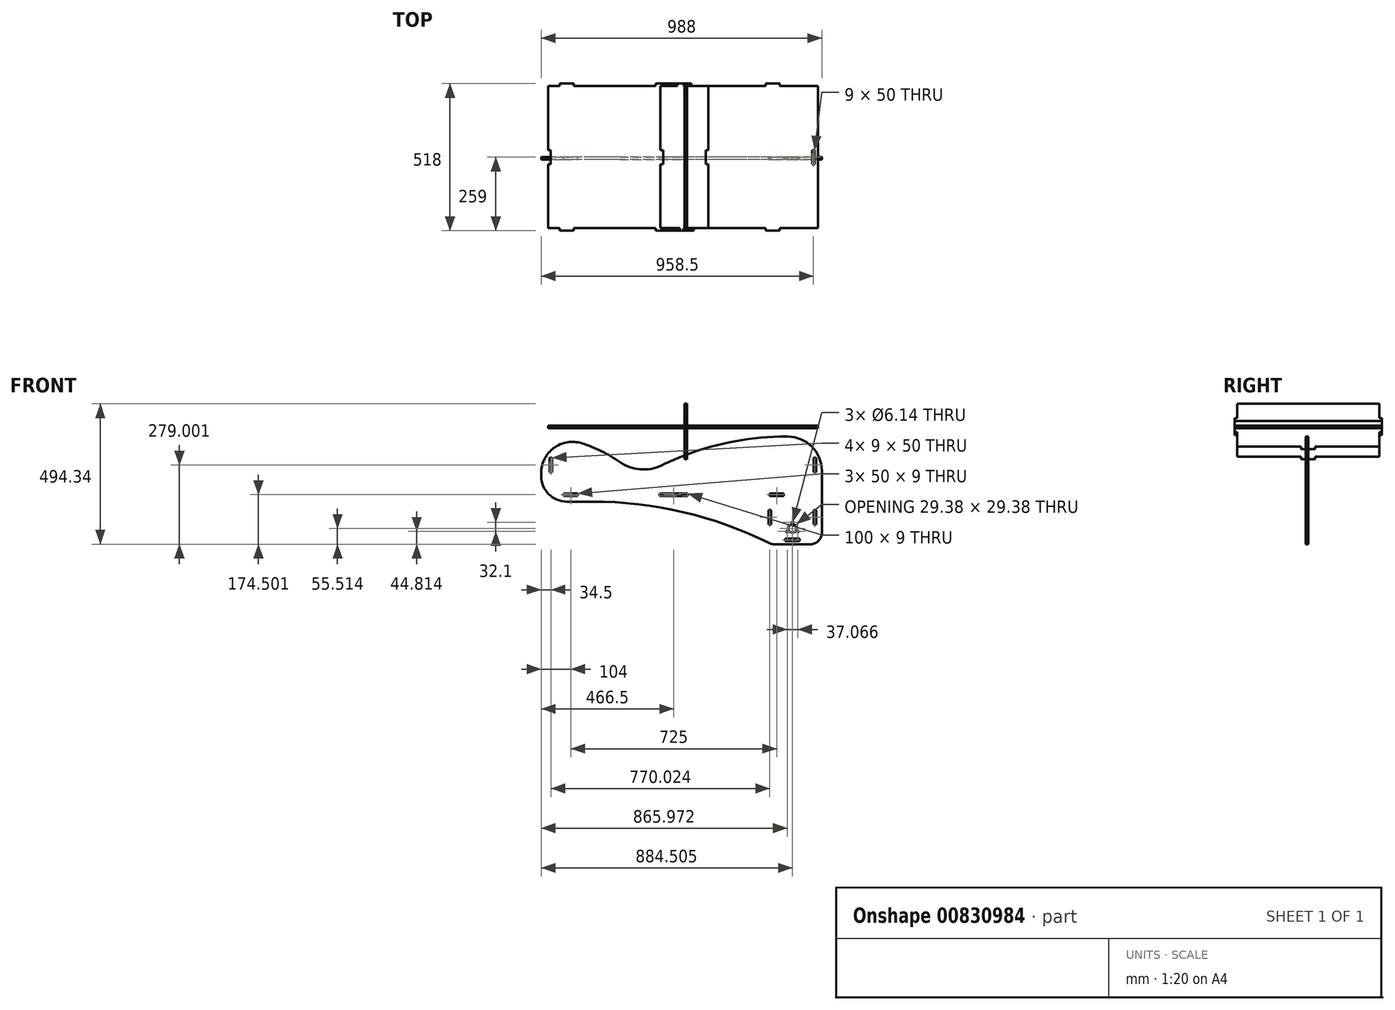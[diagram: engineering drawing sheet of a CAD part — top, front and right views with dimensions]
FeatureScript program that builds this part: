
annotation { "Feature Type Name" : "Feature", "Feature Type Description" : "" }
export const myFeature = defineFeature(function(context is Context, id is Id, definition is map)
    precondition{}
    {
        {
            var Q0;
            Q0=qCreatedBy(makeId("Front.planeOp"),FACE);
            var sketch = newSketch(context, id + "F0", { "sketchPlane" : qUnion([Q0])});
            skPoint(sketch, "E0.middle", {"position": v(0, 0) * mm});
            skLineSegment(sketch, "E1", {"start": v(-87.5, -229.84) * mm, "end": v(-87.5, -238.84) * mm});
            skLineSegment(sketch, "E2", {"start": v(-87.5, -238.84) * mm, "end": v(12.5, -238.84) * mm});
            skLineSegment(sketch, "E3", {"start": v(12.5, -238.84) * mm, "end": v(12.5, -229.84) * mm});
            skLineSegment(sketch, "E4", {"start": v(-425, -229.84) * mm, "end": v(-425, -238.84) * mm});
            skLineSegment(sketch, "E5", {"start": v(-425, -238.84) * mm, "end": v(-375, -238.84) * mm});
            skLineSegment(sketch, "E6", {"start": v(-375, -238.84) * mm, "end": v(-375, -229.84) * mm});
            skLineSegment(sketch, "E7", {"start": v(-425, -229.84) * mm, "end": v(-375, -229.84) * mm});
            skLineSegment(sketch, "E8", {"start": v(-465, -229.84) * mm, "end": v(-465, -230) * mm});
            skLineSegment(sketch, "E9", {"start": v(455.02, -288.84) * mm, "end": v(455.02, -338.84) * mm});
            skLineSegment(sketch, "E10", {"start": v(405.02, -388.84) * mm, "end": v(355.02, -388.84) * mm});
            skLineSegment(sketch, "E11", {"start": v(305.02, -338.84) * mm, "end": v(305.02, -288.84) * mm});
            skLineSegment(sketch, "E12", {"start": v(305.02, -288.84) * mm, "end": v(296.02, -288.84) * mm});
            skLineSegment(sketch, "E13", {"start": v(296.02, -288.84) * mm, "end": v(296.02, -338.84) * mm});
            skLineSegment(sketch, "E14", {"start": v(296.02, -338.84) * mm, "end": v(305.02, -338.84) * mm});
            skLineSegment(sketch, "E15", {"start": v(455.02, -288.84) * mm, "end": v(464.02, -288.84) * mm});
            skLineSegment(sketch, "E16", {"start": v(464.02, -288.84) * mm, "end": v(464.02, -338.84) * mm});
            skLineSegment(sketch, "E17", {"start": v(464.02, -338.84) * mm, "end": v(455.02, -338.84) * mm});
            skLineSegment(sketch, "E18", {"start": v(355.02, -388.84) * mm, "end": v(355.02, -397.84) * mm});
            skLineSegment(sketch, "E19", {"start": v(355.02, -397.84) * mm, "end": v(405.02, -397.84) * mm});
            skLineSegment(sketch, "E20", {"start": v(405.02, -397.84) * mm, "end": v(405.02, -388.84) * mm});
            skPoint(sketch, "E21.start.orphan", {"position": v(380.84, -337.36) * mm});
            skLineSegment(sketch, "E22", {"start": v(380.5, -388.84) * mm, "end": v(380.5, -328.86) * mm});
            skCircle(sketch, "E23", {"center": v(380.5, -353.33) * mm, "radius": 14.7 * mm});
            skCircle(sketch, "E24", {"center": v(380.5, -331.93) * mm, "radius": 3.07 * mm});
            skPoint(sketch, "E24.second.point", {"position": v(380.5, -328.86) * mm});
            skPoint(sketch, "E24.third.point", {"position": v(377.5, -331.28) * mm});
            skPoint(sketch, "E25.end.orphan", {"position": v(380.5, -335) * mm});
            skPoint(sketch, "E25.start.orphan", {"position": v(380.5, -338.64) * mm});
            skCircle(sketch, "E26.1.0", {"center": v(361.97, -364.03) * mm, "radius": 3.07 * mm});
            skPoint(sketch, "E26.1.1", {"position": v(359.31, -365.56) * mm});
            skPoint(sketch, "E26.1.2", {"position": v(362.92, -366.95) * mm});
            skPoint(sketch, "E26.1.3", {"position": v(364.63, -362.5) * mm});
            skCircle(sketch, "E26.2.0", {"center": v(399.04, -364.03) * mm, "radius": 3.07 * mm});
            skPoint(sketch, "E26.2.1", {"position": v(401.7, -365.56) * mm});
            skPoint(sketch, "E26.2.2", {"position": v(401.1, -361.75) * mm});
            skPoint(sketch, "E26.2.3", {"position": v(396.38, -362.5) * mm});
            skLineSegment(sketch, "E27", {"start": v(484, -338.84) * mm, "end": v(484, -408.84) * mm});
            skLineSegment(sketch, "E28", {"start": v(-465, -154.84) * mm, "end": v(-465, -104.84) * mm});
            skLineSegment(sketch, "E29", {"start": v(455, -154.84) * mm, "end": v(455, -104.84) * mm});
            skLineSegment(sketch, "E30", {"start": v(-465, -104.84) * mm, "end": v(-474, -104.84) * mm});
            skLineSegment(sketch, "E31", {"start": v(-474, -104.84) * mm, "end": v(-474, -154.84) * mm});
            skLineSegment(sketch, "E32", {"start": v(-474, -154.84) * mm, "end": v(-465, -154.84) * mm});
            skLineSegment(sketch, "E33", {"start": v(455, -104.84) * mm, "end": v(464, -104.84) * mm});
            skLineSegment(sketch, "E34", {"start": v(464, -154.84) * mm, "end": v(455, -154.84) * mm});
            skLineSegment(sketch, "E35", {"start": v(464, -104.84) * mm, "end": v(464, -154.84) * mm});
            skLineSegment(sketch, "E36", {"start": v(15.12, -258.84) * mm, "end": v(276, -258.84) * mm});
            skLineSegment(sketch, "E37", {"start": v(12.5, -229.84) * mm, "end": v(12.5, -229.84) * mm});
            skLineSegment(sketch, "E38", {"start": v(-87.5, -229.84) * mm, "end": v(-87.5, -229.84) * mm});
            skLineSegment(sketch, "E39", {"start": v(15.12, -258.84) * mm, "end": v(-504, -258.84) * mm});
            skLineSegment(sketch, "E40", {"start": v(-375, -229.84) * mm, "end": v(-375, -229.84) * mm});
            skLineSegment(sketch, "E41", {"start": v(-425, -229.84) * mm, "end": v(-425, -229.84) * mm});
            skLineSegment(sketch, "E42", {"start": v(350, -229.84) * mm, "end": v(300, -229.84) * mm});
            skLineSegment(sketch, "E43", {"start": v(-504, -104.84) * mm, "end": v(-504, -258.84) * mm});
            skLineSegment(sketch, "E44", {"start": v(-504, -104.84) * mm, "end": v(-504, -39.84) * mm});
            skLineSegment(sketch, "E45", {"start": v(455, -29.84) * mm, "end": v(-1.04, -29.84) * mm});
            skLineSegment(sketch, "E46", {"start": v(484, -338.84) * mm, "end": v(484, -229.84) * mm});
            skLineSegment(sketch, "E47", {"start": v(484, -229.84) * mm, "end": v(484, -39.84) * mm});
            skLineSegment(sketch, "E48", {"start": v(474, -29.84) * mm, "end": v(455, -29.84) * mm});
            skLineSegment(sketch, "E49", {"start": v(300, -229.84) * mm, "end": v(300, -238.84) * mm});
            skLineSegment(sketch, "E50", {"start": v(300, -238.84) * mm, "end": v(350, -238.84) * mm});
            skLineSegment(sketch, "E51", {"start": v(350, -238.84) * mm, "end": v(350, -229.84) * mm});
            skLineSegment(sketch, "E52.trimOffspring", {"start": v(-87.5, -229.84) * mm, "end": v(12.5, -229.84) * mm});
            skLineSegment(sketch, "E53.trimOffspring", {"start": v(-375, -229.84) * mm, "end": v(-425, -229.84) * mm});
            skLineSegment(sketch, "E54.trimOffspring", {"start": v(12.5, -229.84) * mm, "end": v(-87.5, -229.84) * mm});
            skLineSegment(sketch, "E55", {"start": v(276, -408.84) * mm, "end": v(484, -408.84) * mm});
            skArc(sketch, "E56", {"start": v(-286.18, -29.84) * mm, "mid": v(-143.6, -145.66) * mm, "end": v(-1.04, -29.84) * mm});
            skLineSegment(sketch, "E57.trimOffspring", {"start": v(-286.18, -29.84) * mm, "end": v(-494, -29.84) * mm});
            skLineSegment(sketch, "E58", {"start": v(-504, -39.84) * mm, "end": v(-504, -29.84) * mm});
            skLineSegment(sketch, "E59", {"start": v(-494, -29.84) * mm, "end": v(-504, -29.84) * mm});
            skLineSegment(sketch, "E60", {"start": v(474, -29.84) * mm, "end": v(484, -29.84) * mm});
            skLineSegment(sketch, "E61", {"start": v(484, -39.84) * mm, "end": v(484, -29.84) * mm});
            skLineSegment(sketch, "E62", {"start": v(276, -258.84) * mm, "end": v(276, -408.84) * mm});
            skSolve(sketch);
        }
        {
            var Q0;
            Q0=qCreatedBy(makeId("Top.planeOp"),FACE);
            var sketch = newSketch(context, id + "F1", { "sketchPlane" : qUnion([Q0])});
            skLineSegment(sketch, "E63.top", {"start": v(470, 250) * mm, "end": v(336, 250) * mm});
            skLineSegment(sketch, "E63.right", {"start": v(-479, -250) * mm, "end": v(-479, -25) * mm});
            skPoint(sketch, "E63.middle", {"position": v(0, 0) * mm});
            skLineSegment(sketch, "E64", {"start": v(-479, -250) * mm, "end": v(-439, -250) * mm});
            skLineSegment(sketch, "E65", {"start": v(-439, -250) * mm, "end": v(-439, -259) * mm});
            skLineSegment(sketch, "E66", {"start": v(-439, -259) * mm, "end": v(-389, -259) * mm});
            skLineSegment(sketch, "E67", {"start": v(-389, -259) * mm, "end": v(-389, -250) * mm});
            skLineSegment(sketch, "E68", {"start": v(-479, 250) * mm, "end": v(-439, 250) * mm});
            skLineSegment(sketch, "E69", {"start": v(-439, 250) * mm, "end": v(-439, 259) * mm});
            skLineSegment(sketch, "E70", {"start": v(-439, 259) * mm, "end": v(-389, 259) * mm});
            skLineSegment(sketch, "E71", {"start": v(-389, 259) * mm, "end": v(-389, 250) * mm});
            skLineSegment(sketch, "E72", {"start": v(-389, 250) * mm, "end": v(-101.5, 250) * mm});
            skLineSegment(sketch, "E73", {"start": v(-101.5, 250) * mm, "end": v(-101.5, 259) * mm});
            skLineSegment(sketch, "E74", {"start": v(-101.5, 259) * mm, "end": v(-1.5, 259) * mm});
            skLineSegment(sketch, "E75", {"start": v(-1.5, 259) * mm, "end": v(-1.5, 250) * mm});
            skLineSegment(sketch, "E76", {"start": v(-1.5, 250) * mm, "end": v(286, 250) * mm});
            skLineSegment(sketch, "E77", {"start": v(286, 250) * mm, "end": v(286, 259) * mm});
            skLineSegment(sketch, "E78", {"start": v(286, 259) * mm, "end": v(336, 259) * mm});
            skLineSegment(sketch, "E79", {"start": v(336, 259) * mm, "end": v(336, 250) * mm});
            skLineSegment(sketch, "E80", {"start": v(-389, -250) * mm, "end": v(-101.5, -250) * mm});
            skLineSegment(sketch, "E81", {"start": v(-101.5, -250) * mm, "end": v(-101.5, -259) * mm});
            skLineSegment(sketch, "E82", {"start": v(-101.5, -259) * mm, "end": v(-1.5, -259) * mm});
            skLineSegment(sketch, "E83", {"start": v(-1.5, -259) * mm, "end": v(-1.5, -250) * mm});
            skLineSegment(sketch, "E84", {"start": v(-1.5, -250) * mm, "end": v(286, -250) * mm});
            skLineSegment(sketch, "E85", {"start": v(286, -250) * mm, "end": v(286, -259) * mm});
            skLineSegment(sketch, "E86", {"start": v(286, -259) * mm, "end": v(336, -259) * mm});
            skLineSegment(sketch, "E87", {"start": v(336, -259) * mm, "end": v(336, -250) * mm});
            skLineSegment(sketch, "E88", {"start": v(-479, -25) * mm, "end": v(-470, -25) * mm});
            skLineSegment(sketch, "E89", {"start": v(-470, -25) * mm, "end": v(-470, 25) * mm});
            skLineSegment(sketch, "E90", {"start": v(-470, 25) * mm, "end": v(-479, 25) * mm});
            skLineSegment(sketch, "E91.trimOffspring", {"start": v(-479, 25) * mm, "end": v(-479, 250) * mm});
            skLineSegment(sketch, "E92.trimOffspring", {"start": v(-439, -250) * mm, "end": v(-479, -250) * mm});
            skLineSegment(sketch, "E93.trimOffspring", {"start": v(-439, 250) * mm, "end": v(-479, 250) * mm});
            skLineSegment(sketch, "E94.trimOffspring", {"start": v(-101.5, 250) * mm, "end": v(-389, 250) * mm});
            skLineSegment(sketch, "E95.trimOffspring", {"start": v(-101.5, -250) * mm, "end": v(-389, -250) * mm});
            skLineSegment(sketch, "E96.trimOffspring", {"start": v(286, -250) * mm, "end": v(-1.5, -250) * mm});
            skLineSegment(sketch, "E97.trimOffspring", {"start": v(286, 250) * mm, "end": v(-1.5, 250) * mm});
            skLineSegment(sketch, "E98", {"start": v(336, -250) * mm, "end": v(470, -250) * mm});
            skLineSegment(sketch, "E99", {"start": v(470, -250) * mm, "end": v(470, 250) * mm});
            skLineSegment(sketch, "E100", {"start": v(-470, 25) * mm, "end": v(450, 25) * mm});
            skLineSegment(sketch, "E101", {"start": v(450, 25) * mm, "end": v(450, -25) * mm});
            skLineSegment(sketch, "E102", {"start": v(450, -25) * mm, "end": v(459, -25) * mm});
            skLineSegment(sketch, "E103", {"start": v(459, -25) * mm, "end": v(459, 25) * mm});
            skLineSegment(sketch, "E104", {"start": v(459, 25) * mm, "end": v(450, 25) * mm});
            skSolve(sketch);
        }
        {
            var Q0;
            Q0=qCreatedBy(makeId("Right.planeOp"),FACE);
            var sketch = newSketch(context, id + "F2", { "sketchPlane" : qUnion([Q0])});
            skLineSegment(sketch, "E105.bottom", {"start": v(-250, -100) * mm, "end": v(-25, -100) * mm});
            skLineSegment(sketch, "E105.left", {"start": v(-250, -100) * mm, "end": v(-250, -25) * mm});
            skLineSegment(sketch, "E105.right", {"start": v(250, -100) * mm, "end": v(250, -25) * mm});
            skPoint(sketch, "E105.middle", {"position": v(0, 0) * mm});
            skLineSegment(sketch, "E106", {"start": v(-250, -25) * mm, "end": v(-259, -25) * mm});
            skLineSegment(sketch, "E107", {"start": v(-259, -25) * mm, "end": v(-259, 25) * mm});
            skLineSegment(sketch, "E108", {"start": v(-259, 25) * mm, "end": v(-250, 25) * mm});
            skLineSegment(sketch, "E109", {"start": v(250, -25) * mm, "end": v(259, -25) * mm});
            skLineSegment(sketch, "E110", {"start": v(259, -25) * mm, "end": v(259, 25) * mm});
            skLineSegment(sketch, "E111", {"start": v(259, 25) * mm, "end": v(250, 25) * mm});
            skLineSegment(sketch, "E112", {"start": v(250, -100) * mm, "end": v(25, -100) * mm});
            skLineSegment(sketch, "E113", {"start": v(25, -100) * mm, "end": v(25, -109) * mm});
            skLineSegment(sketch, "E114", {"start": v(25, -109) * mm, "end": v(-25, -109) * mm});
            skLineSegment(sketch, "E115", {"start": v(-25, -109) * mm, "end": v(-25, -100) * mm});
            skLineSegment(sketch, "E116.trimOffspring", {"start": v(25, -100) * mm, "end": v(250, -100) * mm});
            skLineSegment(sketch, "E117", {"start": v(-250, 25) * mm, "end": v(250, 25) * mm});
            skPoint(sketch, "E118.trimOffspring.end.orphan", {"position": v(-250, 100) * mm});
            skPoint(sketch, "E119.trimOffspring.end.orphan", {"position": v(250, 100) * mm});
            skSolve(sketch);
        }
        {
            var Q0;
            Q0=makeQuery(id+"F1.imprint","IMPRINT",FACE,{"disambiguationData":[TD([[makeQuery(id+"F1.imprint","IMPRINT",EDGE,{"derivedFrom":sQuery(id+"F1.wireOp",EDGE,"E63.top")}),1.0]])]});
            var sketch = newSketch(context, id + "F3", { "sketchPlane" : qUnion([Q0])});
            skLineSegment(sketch, "E120.bottom", {"start": v(84, -250) * mm, "end": v(34, -250) * mm});
            skLineSegment(sketch, "E120.top", {"start": v(84, 250) * mm, "end": v(25, 250) * mm});
            skLineSegment(sketch, "E120.left", {"start": v(84, -250) * mm, "end": v(84, -25) * mm});
            skLineSegment(sketch, "E120.right", {"start": v(-84, -250) * mm, "end": v(-84, -25) * mm});
            skPoint(sketch, "E120.middle", {"position": v(0, 0) * mm});
            skLineSegment(sketch, "E121", {"start": v(25, 250) * mm, "end": v(25, 259) * mm});
            skLineSegment(sketch, "E122", {"start": v(25, 259) * mm, "end": v(-25, 259) * mm});
            skLineSegment(sketch, "E123", {"start": v(-25, 259) * mm, "end": v(-25, 250) * mm});
            skLineSegment(sketch, "E124", {"start": v(34, -250) * mm, "end": v(34, -259) * mm});
            skLineSegment(sketch, "E125", {"start": v(34, -259) * mm, "end": v(-16, -259) * mm});
            skLineSegment(sketch, "E126", {"start": v(-16, -259) * mm, "end": v(-16, -250) * mm});
            skLineSegment(sketch, "E127.trimOffspring", {"start": v(-16, -250) * mm, "end": v(-84, -250) * mm});
            skLineSegment(sketch, "E128", {"start": v(84, -25) * mm, "end": v(75, -25) * mm});
            skLineSegment(sketch, "E129", {"start": v(75, -25) * mm, "end": v(75, 25) * mm});
            skLineSegment(sketch, "E130", {"start": v(75, 25) * mm, "end": v(84, 25) * mm});
            skLineSegment(sketch, "E131", {"start": v(-84, -25) * mm, "end": v(-75, -25) * mm});
            skLineSegment(sketch, "E132", {"start": v(-75, -25) * mm, "end": v(-75, 25) * mm});
            skLineSegment(sketch, "E133", {"start": v(-75, 25) * mm, "end": v(-84, 25) * mm});
            skLineSegment(sketch, "E134.trimOffspring", {"start": v(84, 25) * mm, "end": v(84, 250) * mm});
            skLineSegment(sketch, "E135", {"start": v(-84, 25) * mm, "end": v(-84, 250) * mm});
            skLineSegment(sketch, "E136", {"start": v(-84, 250) * mm, "end": v(-25, 250) * mm});
            skSolve(sketch);
        }
        {
            var Q0;
            Q0=makeQuery(id+"F2.imprint","IMPRINT",FACE,{"disambiguationData":[TD([[makeQuery(id+"F2.imprint","IMPRINT",EDGE,{"derivedFrom":sQuery(id+"F2.wireOp",EDGE,"E105.bottom")}),1.0]])]});
            var sketch = newSketch(context, id + "F4", { "sketchPlane" : qUnion([Q0])});
            skLineSegment(sketch, "E137.top", {"start": v(250, 85.5) * mm, "end": v(25, 85.5) * mm});
            skPoint(sketch, "E137.middle", {"position": v(0, 0) * mm});
            skLineSegment(sketch, "E138", {"start": v(-250, 85.5) * mm, "end": v(-250, 35.5) * mm});
            skLineSegment(sketch, "E139", {"start": v(-250, 35.5) * mm, "end": v(-259, 35.5) * mm});
            skLineSegment(sketch, "E140", {"start": v(-259, 35.5) * mm, "end": v(-259, -14.5) * mm});
            skLineSegment(sketch, "E141", {"start": v(-259, -14.5) * mm, "end": v(-250, -14.5) * mm});
            skLineSegment(sketch, "E142.trimOffspring", {"start": v(-250, 35.5) * mm, "end": v(-250, 85.5) * mm});
            skLineSegment(sketch, "E143", {"start": v(250, 85.5) * mm, "end": v(250, 35.5) * mm});
            skLineSegment(sketch, "E144", {"start": v(250, 35.5) * mm, "end": v(259, 35.5) * mm});
            skLineSegment(sketch, "E145", {"start": v(259, 35.5) * mm, "end": v(259, -14.5) * mm});
            skLineSegment(sketch, "E146", {"start": v(259, -14.5) * mm, "end": v(250, -14.5) * mm});
            skLineSegment(sketch, "E147.trimOffspring", {"start": v(250, 35.5) * mm, "end": v(250, 85.5) * mm});
            skLineSegment(sketch, "E148", {"start": v(-250, 85.5) * mm, "end": v(-25, 85.5) * mm});
            skLineSegment(sketch, "E149.trimOffspring", {"start": v(-25, 85.5) * mm, "end": v(-250, 85.5) * mm});
            skLineSegment(sketch, "E150", {"start": v(250, -14.5) * mm, "end": v(250, -64.5) * mm});
            skLineSegment(sketch, "E151", {"start": v(250, -64.5) * mm, "end": v(25, -64.5) * mm});
            skLineSegment(sketch, "E152", {"start": v(25, -64.5) * mm, "end": v(25, -73.5) * mm});
            skLineSegment(sketch, "E153", {"start": v(25, -73.5) * mm, "end": v(-25, -73.5) * mm});
            skLineSegment(sketch, "E154", {"start": v(-25, -73.5) * mm, "end": v(-25, -64.5) * mm});
            skLineSegment(sketch, "E155", {"start": v(-25, -64.5) * mm, "end": v(-250, -64.5) * mm});
            skLineSegment(sketch, "E156", {"start": v(-250, -64.5) * mm, "end": v(-250, -14.5) * mm});
            skLineSegment(sketch, "E157", {"start": v(25, 85.5) * mm, "end": v(-25, 85.5) * mm});
            skSolve(sketch);
        }
        {
            var Q0;
            Q0 = qSketchRegion(id + "F0", true);
            extrude(context, id + "F5", {"entities" : qUnion([Q0]), "depth" : 9 * mm, "offsetDistance" : 25 * mm});
        }
        {
            var Q0;
            Q0=makeQuery(id+"F5.opExtrude","SWEPT_EDGE",EDGE,{"disambiguationData":[OSD([sQuery(id+"F0.wireOp",EDGE,"cBM0glxq-Qb98-j9on-8ltn-VaepQrnMd0R0"),sQuery(id+"F0.wireOp",EDGE,"E55")])]});
            var Q1;
            Q1=makeQuery(id+"F5.opExtrude","SWEPT_EDGE",EDGE,{"disambiguationData":[OSD([sQuery(id+"F0.wireOp",EDGE,"E27"),sQuery(id+"F0.wireOp",EDGE,"E55")])]});
            fillet(context, id + "F6", {"entities" : qUnion([Q0, Q1]), "radius" : 40 * mm, "tangentPropagation" : true, "allowEdgeOverflow" : false});
        }
        {
            var Q0;
            Q0 = qSketchRegion(id + "F1", true);
            extrude(context, id + "F7", {"entities" : qUnion([Q0]), "depth" : 9 * mm, "offsetDistance" : 25 * mm});
        }
        {
            var Q0;
            Q0 = qSketchRegion(id + "F3", true);
            extrude(context, id + "F8", {"entities" : qUnion([Q0]), "depth" : 9 * mm, "offsetDistance" : 25 * mm});
        }
        {
            var Q0;
            Q0 = qSketchRegion(id + "F4", true);
            extrude(context, id + "F9", {"entities" : qUnion([Q0]), "depth" : 9 * mm, "offsetDistance" : 25 * mm});
        }
        {
            var Q0;
            Q0=makeQuery(id+"F5.opExtrude","SWEPT_EDGE",EDGE,{"disambiguationData":[OSD([sQuery(id+"F0.wireOp",EDGE,"E45"),sQuery(id+"F0.wireOp",EDGE,"E56")])]});
            fillet(context, id + "F10", {"entities" : qUnion([Q0]), "radius" : 1000 * mm, "tangentPropagation" : true, "allowEdgeOverflow" : false});
        }
        {
            var Q0;
            Q0=makeQuery(id+"F5.opExtrude","SWEPT_EDGE",EDGE,{"disambiguationData":[OSD([sQuery(id+"F0.wireOp",EDGE,"E56"),sQuery(id+"F0.wireOp",EDGE,"E57.trimOffspring")])]});
            fillet(context, id + "F11", {"entities" : qUnion([Q0]), "radius" : 500 * mm, "tangentPropagation" : true, "allowEdgeOverflow" : false});
        }
        {
            var Q0;
            Q0=makeQuery(id+"F11.opFillet","BLEND_EDGE",EDGE,{"blendedFrom":[makeQuery(id+"F5.opExtrude","SWEPT_EDGE",EDGE,{"disambiguationData":[OSD([sQuery(id+"F0.wireOp",EDGE,"E56"),sQuery(id+"F0.wireOp",EDGE,"E57.trimOffspring")])]}),makeQuery(id+"F5.opExtrude","SWEPT_FACE",FACE,{"disambiguationData":[OSD([sQuery(id+"F0.wireOp",EDGE,"E43"),sQuery(id+"F0.wireOp",EDGE,"E44"),sQuery(id+"F0.wireOp",EDGE,"E58")])]})],"blendedInto":[makeQuery(id+"F5.opExtrude","SWEPT_FACE",FACE,{"disambiguationData":[OSD([sQuery(id+"F0.wireOp",EDGE,"E43"),sQuery(id+"F0.wireOp",EDGE,"E44"),sQuery(id+"F0.wireOp",EDGE,"E58")])]})]});
            fillet(context, id + "F12", {"entities" : qUnion([Q0]), "radius" : 110 * mm, "tangentPropagation" : true, "allowEdgeOverflow" : false});
        }
        {
            var Q0;
            Q0=makeQuery(id+"F5.opExtrude","SWEPT_EDGE",EDGE,{"disambiguationData":[OSD([sQuery(id+"F0.wireOp",EDGE,"E39"),sQuery(id+"F0.wireOp",EDGE,"E43")])]});
            fillet(context, id + "F13", {"entities" : qUnion([Q0]), "radius" : 90 * mm, "tangentPropagation" : true, "allowEdgeOverflow" : false});
        }
        {
            var Q0;
            Q0=makeQuery(id+"F5.opExtrude","SWEPT_EDGE",EDGE,{"disambiguationData":[OSD([sQuery(id+"F0.wireOp",EDGE,"E36"),sQuery(id+"F0.wireOp",EDGE,"WXEozqvh-aRw7-6Bn3-RnxX-178lBw6AXMKx")])]});
            fillet(context, id + "F14", {"entities" : qUnion([Q0]), "radius" : 1400 * mm, "tangentPropagation" : true, "allowEdgeOverflow" : false});
        }
        {
            var Q0;
            Q0=makeQuery(id+"F5.opExtrude","SWEPT_EDGE",EDGE,{"disambiguationData":[OSD([sQuery(id+"F0.wireOp",EDGE,"E60"),sQuery(id+"F0.wireOp",EDGE,"E61")])]});
            fillet(context, id + "F15", {"entities" : qUnion([Q0]), "radius" : 120 * mm, "tangentPropagation" : true, "allowEdgeOverflow" : false});
        }
        {
            var Q0;
            Q0 = qSketchRegion(id + "F2", true);
            extrude(context, id + "F16", {"entities" : qUnion([Q0]), "depth" : 9 * mm, "offsetDistance" : 25 * mm});
        }
    });
